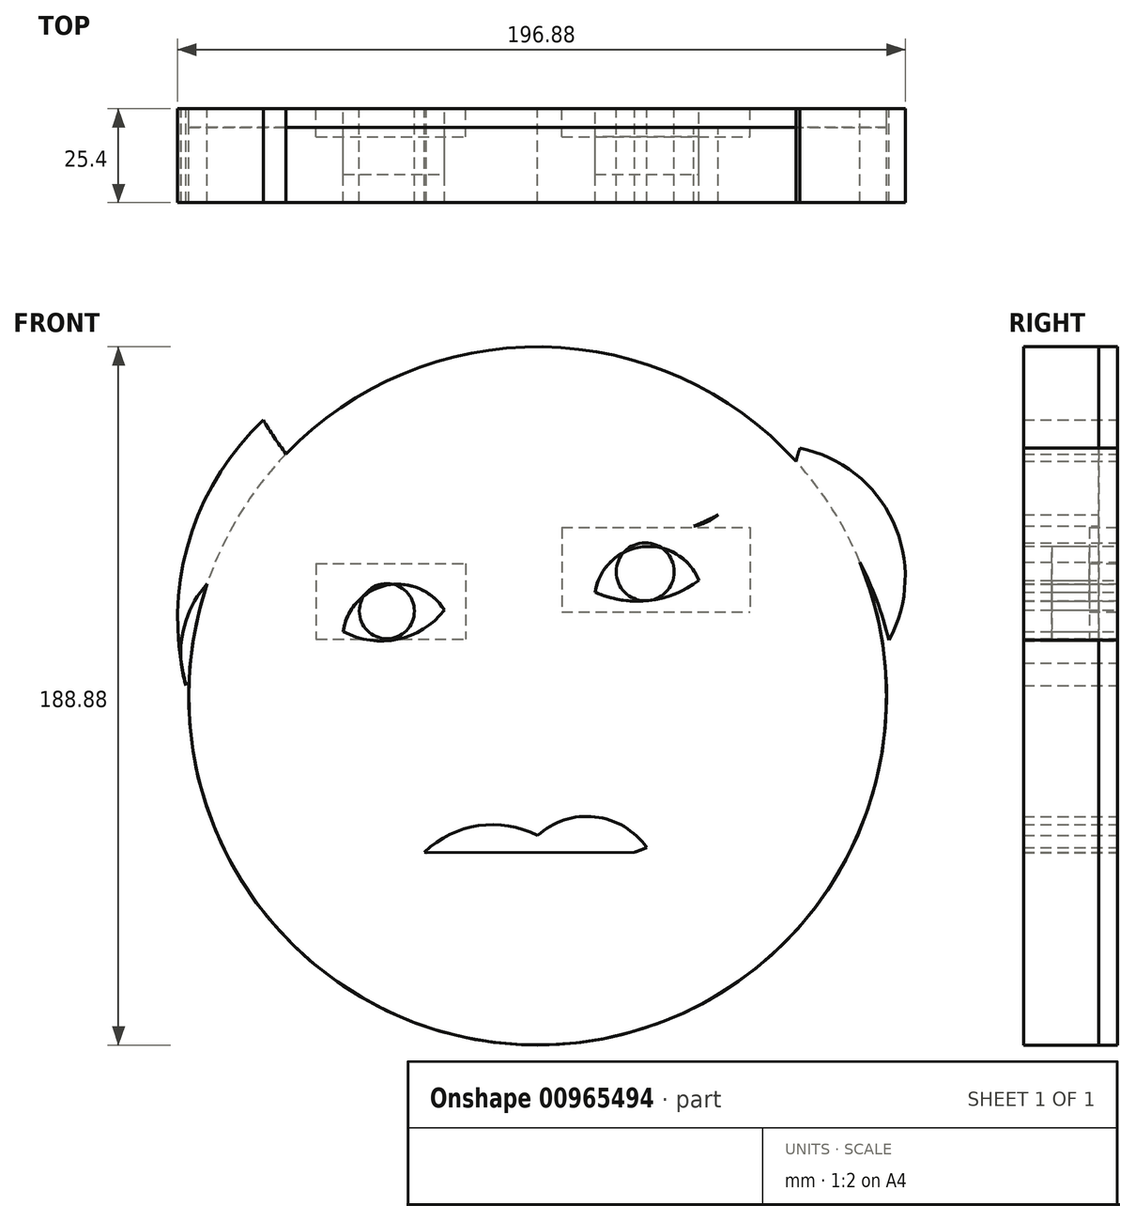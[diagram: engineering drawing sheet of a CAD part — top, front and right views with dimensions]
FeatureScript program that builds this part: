
annotation { "Feature Type Name" : "Feature", "Feature Type Description" : "" }
export const myFeature = defineFeature(function(context is Context, id is Id, definition is map)
    precondition{}
    {
        {
            var Q0;
            Q0=qCreatedBy(makeId("Front.planeOp"),FACE);
            var sketch = newSketch(context, id + "F0", { "sketchPlane" : qUnion([Q0])});
            skCircle(sketch, "E0", {"center": v(0, 0) * mm, "radius": 94.44 * mm});
            skSolve(sketch);
        }
        {
            var Q0;
            Q0=makeQuery(id+"F0.imprint","IMPRINT",FACE,{"disambiguationData":[TD([[makeQuery(id+"F0.imprint","IMPRINT",EDGE,{"derivedFrom":sQuery(id+"F0.wireOp",EDGE,"E0")}),1.0]])]});
            var sketch = newSketch(context, id + "F1", { "sketchPlane" : qUnion([Q0])});
            skArc(sketch, "E1", {"start": v(-25.24, 23.22) * mm, "mid": v(-40.94, 29.9) * mm, "end": v(-52.61, 17.45) * mm});
            skArc(sketch, "E2", {"start": v(43.61, 31.3) * mm, "mid": v(28.37, 40.36) * mm, "end": v(15.57, 28.08) * mm});
            skArc(sketch, "E3", {"start": v(-52.61, 17.45) * mm, "mid": v(-37.87, 15.34) * mm, "end": v(-25.24, 23.22) * mm});
            skArc(sketch, "E4", {"start": v(15.57, 28.08) * mm, "mid": v(30.04, 25.8) * mm, "end": v(43.61, 31.3) * mm});
            skSolve(sketch);
        }
        {
            var Q0;
            Q0=makeQuery(id+"F0.imprint","IMPRINT",FACE,{"disambiguationData":[TD([[makeQuery(id+"F0.imprint","IMPRINT",EDGE,{"derivedFrom":sQuery(id+"F0.wireOp",EDGE,"E0")}),1.0]])]});
            var sketch = newSketch(context, id + "F2", { "sketchPlane" : qUnion([Q0])});
            skLineSegment(sketch, "E5", {"start": v(-19.96, 37.4) * mm, "end": v(-12.17, 21.46) * mm});
            skLineSegment(sketch, "E6", {"start": v(-12.17, 21.46) * mm, "end": v(-9.96, -5.89) * mm});
            skLineSegment(sketch, "E7", {"start": v(11.7, 41.57) * mm, "end": v(4.56, 25.55) * mm});
            skLineSegment(sketch, "E8", {"start": v(4.56, 25.55) * mm, "end": v(7.48, -5.38) * mm});
            skArc(sketch, "E9", {"start": v(-9.96, -5.89) * mm, "mid": v(-18.26, -11.02) * mm, "end": v(-13.66, -19.62) * mm});
            skArc(sketch, "E10", {"start": v(10.7, -18.08) * mm, "mid": v(16.85, -9.76) * mm, "end": v(7.48, -5.38) * mm});
            skArc(sketch, "E11", {"start": v(-9.96, -14.72) * mm, "mid": v(-1.15, -27.52) * mm, "end": v(7.48, -14.6) * mm});
            skLineSegment(sketch, "E12", {"start": v(-19.96, 37.4) * mm, "end": v(11.7, 41.57) * mm});
            skLineSegment(sketch, "E13", {"start": v(-13.66, -19.62) * mm, "end": v(-9.96, -14.72) * mm});
            skLineSegment(sketch, "E14", {"start": v(10.7, -18.08) * mm, "end": v(7.48, -14.6) * mm});
            skSolve(sketch);
        }
        {
            var Q0;
            Q0=makeQuery(id+"F0.imprint","IMPRINT",FACE,{"disambiguationData":[TD([[makeQuery(id+"F0.imprint","IMPRINT",EDGE,{"derivedFrom":sQuery(id+"F0.wireOp",EDGE,"E0")}),1.0]])]});
            var sketch = newSketch(context, id + "F3", { "sketchPlane" : qUnion([Q0])});
            skCircle(sketch, "E15", {"center": v(-40.8, 22.94) * mm, "radius": 7.45 * mm});
            skPoint(sketch, "E15.first.point", {"position": v(-45.8, 28.45) * mm});
            skPoint(sketch, "E15.second.point", {"position": v(-35.15, 18.07) * mm});
            skPoint(sketch, "E15.third.point", {"position": v(-40.81, 15.49) * mm});
            skCircle(sketch, "E16", {"center": v(29.12, 33.57) * mm, "radius": 7.84 * mm});
            skPoint(sketch, "E16.first.point", {"position": v(22.7, 38.07) * mm});
            skPoint(sketch, "E16.second.point", {"position": v(35.5, 29.02) * mm});
            skPoint(sketch, "E16.third.point", {"position": v(32.74, 40.52) * mm});
            skSolve(sketch);
        }
        {
            var Q0;
            Q0=makeQuery(id+"F0.imprint","IMPRINT",FACE,{"disambiguationData":[TD([[makeQuery(id+"F0.imprint","IMPRINT",EDGE,{"derivedFrom":sQuery(id+"F0.wireOp",EDGE,"E0")}),1.0]])]});
            var sketch = newSketch(context, id + "F4", { "sketchPlane" : qUnion([Q0])});
            skLineSegment(sketch, "E17.bottom", {"start": v(-59.95, 35.82) * mm, "end": v(-19.45, 35.82) * mm});
            skLineSegment(sketch, "E17.top", {"start": v(-59.95, 15.3) * mm, "end": v(-19.45, 15.3) * mm});
            skLineSegment(sketch, "E17.left", {"start": v(-59.95, 35.82) * mm, "end": v(-59.95, 15.3) * mm});
            skLineSegment(sketch, "E17.right", {"start": v(-19.45, 35.82) * mm, "end": v(-19.45, 15.3) * mm});
            skLineSegment(sketch, "E18.bottom", {"start": v(6.5, 45.57) * mm, "end": v(57.54, 45.57) * mm});
            skLineSegment(sketch, "E18.top", {"start": v(6.5, 22.77) * mm, "end": v(57.54, 22.77) * mm});
            skLineSegment(sketch, "E18.left", {"start": v(6.5, 45.57) * mm, "end": v(6.5, 22.77) * mm});
            skLineSegment(sketch, "E18.right", {"start": v(57.54, 45.57) * mm, "end": v(57.54, 22.77) * mm});
            skLineSegment(sketch, "E19", {"start": v(-19.45, 25.56) * mm, "end": v(6.5, 34.17) * mm});
            skLineSegment(sketch, "E20", {"start": v(-59.95, 25.56) * mm, "end": v(-93.19, 0) * mm});
            skLineSegment(sketch, "E21", {"start": v(57.54, 34.17) * mm, "end": v(85.5, 30.56) * mm});
            skLineSegment(sketch, "E22.bottom", {"start": v(-55.75, 35.82) * mm, "end": v(-23.5, 35.82) * mm});
            skLineSegment(sketch, "E22.top", {"start": v(-55.75, 19.68) * mm, "end": v(-23.5, 19.68) * mm});
            skLineSegment(sketch, "E22.left", {"start": v(-55.75, 35.82) * mm, "end": v(-55.75, 19.68) * mm});
            skLineSegment(sketch, "E22.right", {"start": v(-23.5, 35.82) * mm, "end": v(-23.5, 19.68) * mm});
            skPoint(sketch, "E23.oppositeSnap0", {"position": v(-6.47, 29.87) * mm});
            skLineSegment(sketch, "E23.bottom", {"start": v(12.28, 45.57) * mm, "end": v(53.75, 45.57) * mm});
            skLineSegment(sketch, "E23.top", {"start": v(12.28, 29.87) * mm, "end": v(53.75, 29.87) * mm});
            skLineSegment(sketch, "E23.left", {"start": v(12.28, 45.57) * mm, "end": v(12.28, 29.87) * mm});
            skLineSegment(sketch, "E23.right", {"start": v(53.75, 45.57) * mm, "end": v(53.75, 29.87) * mm});
            skSolve(sketch);
        }
        {
            var Q0;
            Q0=makeQuery(id+"F0.imprint","IMPRINT",FACE,{"disambiguationData":[TD([[makeQuery(id+"F0.imprint","IMPRINT",EDGE,{"derivedFrom":sQuery(id+"F0.wireOp",EDGE,"E0")}),1.0]])]});
            var sketch = newSketch(context, id + "F5", { "sketchPlane" : qUnion([Q0])});
            skArc(sketch, "E24", {"start": v(0, -37.76) * mm, "mid": v(-16, -35.1) * mm, "end": v(-30.58, -42.23) * mm});
            skArc(sketch, "E25", {"start": v(29.53, -41.05) * mm, "mid": v(15.51, -32.7) * mm, "end": v(0, -37.76) * mm});
            skLineSegment(sketch, "E26", {"start": v(-46.49, -42.4) * mm, "end": v(53.86, -42.23) * mm});
            skArc(sketch, "E27", {"start": v(-30.58, -42.23) * mm, "mid": v(-0.42, -47.06) * mm, "end": v(29.53, -41.05) * mm});
            skSolve(sketch);
        }
        {
            var Q0;
            Q0=makeQuery(id+"F1.imprint","IMPRINT",FACE,{"disambiguationData":[TD([[makeQuery(id+"F1.imprint","IMPRINT",EDGE,{"derivedFrom":sQuery(id+"F1.wireOp",EDGE,"E1")}),-1.0]])]});
            var sketch = newSketch(context, id + "F6", { "sketchPlane" : qUnion([Q0])});
            skArc(sketch, "E28", {"start": v(-74.24, 74.68) * mm, "mid": v(-53.91, 50.48) * mm, "end": v(-26.76, 34.3) * mm});
            skArc(sketch, "E29", {"start": v(-37.76, 59.42) * mm, "mid": v(-34.56, 45.85) * mm, "end": v(-26.76, 34.3) * mm});
            skArc(sketch, "E30", {"start": v(-37.76, 59.42) * mm, "mid": v(-28.4, 43.28) * mm, "end": v(-14.23, 31.15) * mm});
            skArc(sketch, "E31", {"start": v(-21.76, 48.99) * mm, "mid": v(-20.75, 38.9) * mm, "end": v(-14.23, 31.15) * mm});
            skArc(sketch, "E32", {"start": v(-21.76, 48.99) * mm, "mid": v(13.53, 40.25) * mm, "end": v(48.81, 48.99) * mm});
            skArc(sketch, "E33", {"start": v(27.24, 59.42) * mm, "mid": v(34.57, 47.06) * mm, "end": v(48.81, 48.99) * mm});
            skArc(sketch, "E34", {"start": v(71, 48.99) * mm, "mid": v(50.88, 61.6) * mm, "end": v(27.24, 59.42) * mm});
            skArc(sketch, "E35", {"start": v(73.3, 71.78) * mm, "mid": v(69.52, 60.65) * mm, "end": v(71, 48.99) * mm});
            skArc(sketch, "E36", {"start": v(73.3, 71.78) * mm, "mid": v(1.27, 98.25) * mm, "end": v(-71.75, 74.68) * mm});
            skArc(sketch, "E37", {"start": v(-74.24, 74.68) * mm, "mid": v(-94.46, 41.56) * mm, "end": v(-95.15, 2.76) * mm});
            skArc(sketch, "E38", {"start": v(-78.72, 37.9) * mm, "mid": v(-93.88, 23.58) * mm, "end": v(-95.15, 2.76) * mm});
            skArc(sketch, "E39", {"start": v(-78.72, 37.9) * mm, "mid": v(-84.59, 28.87) * mm, "end": v(-78.72, 19.85) * mm});
            skArc(sketch, "E40", {"start": v(-58.96, 55.1) * mm, "mid": v(-73.18, 39.9) * mm, "end": v(-78.72, 19.85) * mm});
            skArc(sketch, "E41", {"start": v(95.1, 15.1) * mm, "mid": v(96.18, 47.16) * mm, "end": v(71, 67.04) * mm});
            skArc(sketch, "E42", {"start": v(95.1, 15.1) * mm, "mid": v(85.86, 38.78) * mm, "end": v(71, 59.42) * mm});
            skSolve(sketch);
        }
        {
            var Q0;
            {var subQ0=sQuery(id+"F6.wireOp",EDGE,"E38");var subQ1=sQuery(id+"F6.wireOp",EDGE,"E37");var subQ2=makeQuery(id+"F6.imprint","INTERSECT",VERTEX,{"disambiguationData":[OD(0.0)],"derivedFrom":[subQ1,subQ0]});Q0=makeQuery(id+"F6.imprint","IMPRINT",FACE,{"disambiguationData":[TD([[makeQuery(id+"F6.imprint","IMPRINT",EDGE,{"disambiguationData":[TD([[subQ2,1.0]])],"derivedFrom":subQ1}),-1.0]])]});}
            var Q1;
            {var subQ0=sQuery(id+"F6.wireOp",EDGE,"E33");var subQ1=sQuery(id+"F6.wireOp",EDGE,"E32");var subQ2=makeQuery(id+"F6.imprint","INTERSECT",VERTEX,{"disambiguationData":[OD(0.0)],"derivedFrom":[subQ1,subQ0]});Q1=makeQuery(id+"F6.imprint","IMPRINT",FACE,{"disambiguationData":[TD([[makeQuery(id+"F6.imprint","IMPRINT",EDGE,{"disambiguationData":[TD([[subQ2,1.0]])],"derivedFrom":subQ1}),-1.0]])]});}
            var Q2;
            {var subQ1=sQuery(id+"F6.wireOp",EDGE,"E39");Q2=makeQuery(id+"F6.imprint","IMPRINT",FACE,{"disambiguationData":[TD([[makeQuery(id+"F6.imprint","IMPRINT",EDGE,{"derivedFrom":subQ1}),1.0]])]});}
            var Q3;
            {var subQ0=sQuery(id+"F6.wireOp",EDGE,"E37");var subQ1=sQuery(id+"F6.wireOp",EDGE,"E28");var subQ2=makeQuery(id+"F6.imprint","INTERSECT",VERTEX,{"derivedFrom":[subQ1,subQ0]});Q3=makeQuery(id+"F6.imprint","IMPRINT",FACE,{"disambiguationData":[TD([[makeQuery(id+"F6.imprint","IMPRINT",EDGE,{"disambiguationData":[TD([[subQ2,-1.0]])],"derivedFrom":subQ1}),-1.0]])]});}
            var Q4;
            {var subQ0=sQuery(id+"F6.wireOp",EDGE,"E41");Q4=makeQuery(id+"F6.imprint","IMPRINT",FACE,{"disambiguationData":[TD([[makeQuery(id+"F6.imprint","IMPRINT",EDGE,{"derivedFrom":subQ0}),1.0]])]});}
            var Q5;
            {var subQ0=sQuery(id+"F6.wireOp",EDGE,"E29");Q5=makeQuery(id+"F6.imprint","IMPRINT",FACE,{"disambiguationData":[TD([[makeQuery(id+"F6.imprint","IMPRINT",EDGE,{"derivedFrom":subQ0}),-1.0]])]});}
            var Q6;
            Q6=makeQuery(id+"F3.imprint","IMPRINT",FACE,{"disambiguationData":[TD([[makeQuery(id+"F3.imprint","IMPRINT",EDGE,{"derivedFrom":sQuery(id+"F3.wireOp",EDGE,"E15")}),1.0]])]});
            var Q7;
            Q7=makeQuery(id+"F3.imprint","IMPRINT",FACE,{"disambiguationData":[TD([[makeQuery(id+"F3.imprint","IMPRINT",EDGE,{"derivedFrom":sQuery(id+"F3.wireOp",EDGE,"E16")}),1.0]])]});
            extrude(context, id + "F7", {"entities" : qUnion([Q0, Q1, Q2, Q3, Q4, Q5, Q6, Q7]), "depth" : 25.4 * mm, "offsetDistance" : 25.4 * mm});
        }
        {
            var Q0;
            Q0 = qSketchRegion(id + "F2", true);
            extrude(context, id + "F8", {"entities" : qUnion([Q0]), "operationType" : NewBodyOperationType.ADD, "depth" : 25.4 * mm, "offsetDistance" : 25.4 * mm});
        }
        {
            var Q0;
            Q0 = qSketchRegion(id + "F1", true);
            extrude(context, id + "F9", {"entities" : qUnion([Q0]), "depth" : 17.78 * mm, "offsetDistance" : 25.4 * mm});
        }
        {
            var Q0;
            {var subQ1=sQuery(id+"F5.wireOp",EDGE,"E24");Q0=makeQuery(id+"F5.imprint","IMPRINT",FACE,{"disambiguationData":[TD([[makeQuery(id+"F5.imprint","IMPRINT",EDGE,{"derivedFrom":subQ1}),1.0]])]});}
            extrude(context, id + "F10", {"entities" : qUnion([Q0]), "depth" : 25.4 * mm, "offsetDistance" : 25.4 * mm});
        }
        {
            var Q0;
            Q0 = qSketchRegion(id + "F4", true);
            extrude(context, id + "F11", {"entities" : qUnion([Q0]), "depth" : 7.62 * mm, "offsetDistance" : 25.4 * mm});
        }
        {
            var Q0;
            Q0 = qSketchRegion(id + "F0", true);
            extrude(context, id + "F12", {"entities" : qUnion([Q0]), "depth" : 5.08 * mm, "offsetDistance" : 25.4 * mm});
        }
    });
